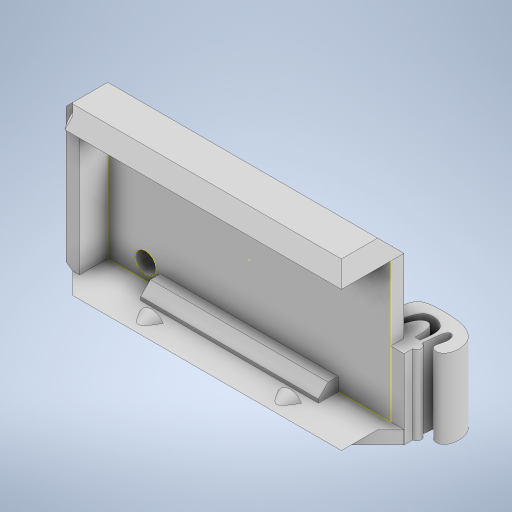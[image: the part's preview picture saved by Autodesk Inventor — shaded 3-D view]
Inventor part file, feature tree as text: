
AUTODESK INVENTOR PART (.ipt)
format: ipt  version: 2023 (Build 270158030, 158C)  size: 781,824 bytes
history: native  units: mm
features: extrude x11, sketch x10, chamfer x8, other x6, projected_geometry x5, mirror x3, plane x2, reference x1
ambient origin geometry x8: Origin, YZ Plane, XZ Plane, XY Plane, X Axis, Y Axis, Z Axis, Center Point
bodies: Solid1 (feature_tree)
feature tree (46):
  other  "Blocks"
  sketch  "Sketch1"  dims[d0=2.0mm d1=0.0mm d3=1.985343mm]
  extrude  "Extrusion1"  Depth=1.985343mm
  plane  "Work Plane1"
  extrude  "Extrusion2"  Depth=23.5mm
  mirror  "Mirror1"
  extrude  "Extrusion6"  Depth=3.0mm
  extrude  "Extrusion7"  Depth=4.630585mm
  extrude  "Extrusion8"  Depth=0.917895mm
  mirror  "Mirror2"
  extrude  "Extrusion9"  Depth=1.460869mm
  plane  "Work Plane4"
  extrude  "Extrusion11"  Depth=2.954284mm
  extrude  "Extrusion12"  Depth=0.593847mm
  mirror  "Mirror3"
  extrude  "Extrusion13"  Depth=2.0mm
  chamfer  "Chamfer5"  Distance=2.0mm
  chamfer  "Chamfer6"  Distance=2.0mm
  chamfer  "Chamfer7"  Distance=8.0mm
  chamfer  "Chamfer8"  Distance=8.0mm
  extrude  "Extrusion14"  Depth=2.0mm TaperAngle=0.0deg
  extrude  "Extrusion15"  Depth=1.3mm
  chamfer  "Chamfer9"  Distance=3.0mm
  chamfer  "Chamfer10"  Distance=3.0mm
  chamfer  "Chamfer11"  Distance=4.0mm
  chamfer  "Chamfer12"  Distance=3.0mm
  reference  "Reference1"
  sketch  "Sketch2"  dims[d4=10.0mm d5=0.0mm d41=23.5mm]
  other  "DIN-rail-mount"
  sketch  "Sketch6"  dims[d43=3.0mm d44=0.630858mm]
  sketch  "Sketch8"  dims[d45=17.780726mm d46=4.630585mm]
  sketch  "Sketch9"  dims[d47=6.409146mm d48=0.917895mm]
  projected_geometry  "Projected Loop1"
  sketch  "Sketch12"  dims[d49=1.257608mm d50=1.460869mm]
  projected_geometry  "Projected Loop5"
  sketch  "Sketch13"  dims[d51=0.803745mm d52=2.954284mm]
  projected_geometry  "Projected Loop6"
  sketch  "Sketch14"  dims[d53=0.7465mm d54=0.593847mm]
  projected_geometry  "Projected Loop7"
  projected_geometry  "Projected Loop8"
  sketch  "Sketch15"  dims[d55=0.0mm d56=0.0mm d57=17.5mm d58=2.0mm d59=0.0mm]
  other  "board"
  sketch  "Sketch16"  dims[d60=3.0mm d61=2.0mm d62=0.0mm d63=8.0mm d64=8.0mm d65=10.0mm d66=0.0mm d67=1.3mm d74=3.0mm d75=3.0mm d76=4.0mm d77=3.0mm d78=12.0mm d79=-4.537856mm d80=12.0mm d81=0.0mm d82=0.0mm d83=0.0mm d84=2.0mm d85=2.0mm d86=45.0deg d88=1.5mm d89=2.0mm d90=45.0deg d91=1.5mm d92=2.0mm d93=45.0deg d94=2.0mm d95=2.0mm d96=45.0deg d97=21.0mm d98=43.0mm d99=1.3mm d100=0.0mm d101=1.3mm d102=0.0mm d103=1.0mm d104=2.0mm d105=45.0deg d106=2.0mm d107=2.0mm d108=45.0deg d109=3.8mm d110=2.0mm d111=45.0deg d112=1.0mm d113=2.0mm d114=45.0deg]
  other  "buck-converter-din-rail-mount.iam"
  other  "Power Buck Converter:1"
  other  "DIN-rail-mount:1"
